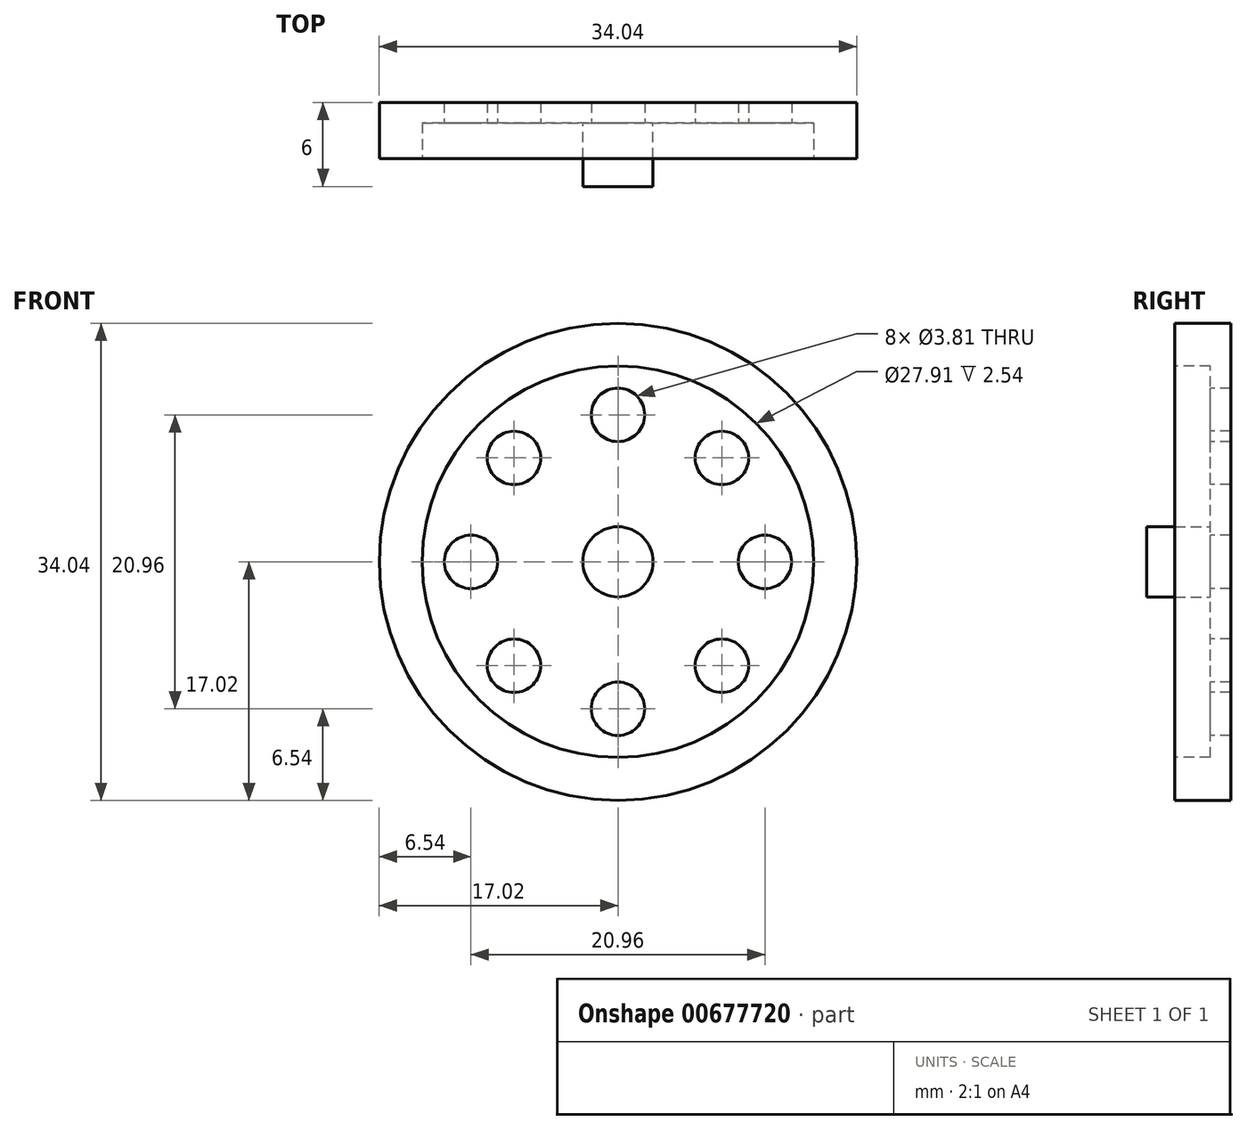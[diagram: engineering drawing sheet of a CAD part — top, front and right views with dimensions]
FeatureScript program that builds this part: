
annotation { "Feature Type Name" : "Feature", "Feature Type Description" : "" }
export const myFeature = defineFeature(function(context is Context, id is Id, definition is map)
    precondition{}
    {
        {
            var Q0;
            Q0=qCreatedBy(makeId("Front.planeOp"),FACE);
            var sketch = newSketch(context, id + "F0", { "sketchPlane" : qUnion([Q0])});
            skCircle(sketch, "E0", {"center": v(0, 0) * mm, "radius": 17.02 * mm});
            skSolve(sketch);
        }
        {
            var Q0;
            Q0 = qSketchRegion(id + "F0", true);
            extrude(context, id + "F1", {"entities" : qUnion([Q0]), "oppositeDirection" : true, "depth" : 4 * mm, "offsetDistance" : 25 * mm});
        }
        {
            var Q0;
            Q0=makeQuery(id+"F1.opExtrude","CAP_FACE",FACE,{"disambiguationData":[OSD([sQuery(id+"F0.wireOp",EDGE,"E0")])],"isStart":true});
            var sketch = newSketch(context, id + "F2", { "sketchPlane" : qUnion([Q0])});
            skCircle(sketch, "E1", {"center": v(0, 0) * mm, "radius": 6 * mm});
            skSolve(sketch);
        }
        {
            var Q0;
            Q0=sQuery(id+"F2.wireOp",EDGE,"E1");
            extrude(context, id + "F3", {"bodyType" : ToolBodyType.SURFACE, "surfaceEntities" : qUnion([Q0]), "oppositeDirection" : true, "depth" : 4 * mm, "offsetDistance" : 25 * mm});
        }
        {
            var Q0;
            Q0=qCreatedBy(makeId("Front.planeOp"),FACE);
            var sketch = newSketch(context, id + "F4", { "sketchPlane" : qUnion([Q0])});
            skCircle(sketch, "E2", {"center": v(0, 0) * mm, "radius": 2.5 * mm});
            skSolve(sketch);
        }
        {
            var Q0;
            Q0 = qSketchRegion(id + "F4", true);
            extrude(context, id + "F5", {"entities" : qUnion([Q0]), "operationType" : NewBodyOperationType.ADD, "depth" : 2 * mm, "offsetDistance" : 25 * mm});
        }
        {
            var Q0;
            Q0=makeQuery(id+"F1.opExtrude","CAP_FACE",FACE,{"disambiguationData":[OSD([sQuery(id+"F0.wireOp",EDGE,"E0")])],"isStart":false});
            var sketch = newSketch(context, id + "F6", { "sketchPlane" : qUnion([Q0])});
            skSolve(sketch);
        }
        {
            var Q0;
            Q0=makeQuery(id+"F1.opExtrude","CAP_FACE",FACE,{"disambiguationData":[OSD([sQuery(id+"F0.wireOp",EDGE,"E0")])],"isStart":true});
            var sketch = newSketch(context, id + "F7", { "sketchPlane" : qUnion([Q0])});
            skCircle(sketch, "E3", {"center": v(0, 10.48) * mm, "radius": 1.9 * mm});
            skCircle(sketch, "E4.1.0", {"center": v(-7.41, 7.41) * mm, "radius": 1.9 * mm});
            skCircle(sketch, "E4.2.0", {"center": v(-10.48, 0) * mm, "radius": 1.9 * mm});
            skCircle(sketch, "E4.3.0", {"center": v(-7.41, -7.41) * mm, "radius": 1.9 * mm});
            skCircle(sketch, "E4.4.0", {"center": v(0, -10.48) * mm, "radius": 1.9 * mm});
            skCircle(sketch, "E4.5.0", {"center": v(7.41, -7.41) * mm, "radius": 1.9 * mm});
            skCircle(sketch, "E4.6.0", {"center": v(10.48, 0) * mm, "radius": 1.9 * mm});
            skCircle(sketch, "E4.7.0", {"center": v(7.41, 7.41) * mm, "radius": 1.9 * mm});
            skPoint(sketch, "E4.center", {"position": v(0, 0) * mm});
            skSolve(sketch);
        }
        {
            var Q0;
            Q0=makeQuery(id+"F7.imprint","IMPRINT",FACE,{"disambiguationData":[TD([[makeQuery(id+"F7.imprint","IMPRINT",EDGE,{"derivedFrom":sQuery(id+"F7.wireOp",EDGE,"E4.1.0")}),1.0]])]});
            var Q1;
            Q1=makeQuery(id+"F7.imprint","IMPRINT",FACE,{"disambiguationData":[TD([[makeQuery(id+"F7.imprint","IMPRINT",EDGE,{"derivedFrom":sQuery(id+"F7.wireOp",EDGE,"E3")}),1.0]])]});
            var Q2;
            Q2=makeQuery(id+"F7.imprint","IMPRINT",FACE,{"disambiguationData":[TD([[makeQuery(id+"F7.imprint","IMPRINT",EDGE,{"derivedFrom":sQuery(id+"F7.wireOp",EDGE,"E4.7.0")}),1.0]])]});
            var Q3;
            Q3=makeQuery(id+"F7.imprint","IMPRINT",FACE,{"disambiguationData":[TD([[makeQuery(id+"F7.imprint","IMPRINT",EDGE,{"derivedFrom":sQuery(id+"F7.wireOp",EDGE,"E4.6.0")}),1.0]])]});
            var Q4;
            Q4=makeQuery(id+"F7.imprint","IMPRINT",FACE,{"disambiguationData":[TD([[makeQuery(id+"F7.imprint","IMPRINT",EDGE,{"derivedFrom":sQuery(id+"F7.wireOp",EDGE,"E4.5.0")}),1.0]])]});
            var Q5;
            Q5=makeQuery(id+"F7.imprint","IMPRINT",FACE,{"disambiguationData":[TD([[makeQuery(id+"F7.imprint","IMPRINT",EDGE,{"derivedFrom":sQuery(id+"F7.wireOp",EDGE,"E4.4.0")}),1.0]])]});
            var Q6;
            Q6=makeQuery(id+"F7.imprint","IMPRINT",FACE,{"disambiguationData":[TD([[makeQuery(id+"F7.imprint","IMPRINT",EDGE,{"derivedFrom":sQuery(id+"F7.wireOp",EDGE,"E4.3.0")}),1.0]])]});
            var Q7;
            Q7=makeQuery(id+"F7.imprint","IMPRINT",FACE,{"disambiguationData":[TD([[makeQuery(id+"F7.imprint","IMPRINT",EDGE,{"derivedFrom":sQuery(id+"F7.wireOp",EDGE,"E4.2.0")}),1.0]])]});
            extrude(context, id + "F8", {"entities" : qUnion([Q0, Q1, Q2, Q3, Q4, Q5, Q6, Q7]), "operationType" : NewBodyOperationType.REMOVE, "oppositeDirection" : true, "depth" : 25.4 * mm, "offsetDistance" : 25.4 * mm});
        }
        {
            var Q0;
            Q0=makeQuery(id+"F1.opExtrude","CAP_FACE",FACE,{"disambiguationData":[OSD([sQuery(id+"F0.wireOp",EDGE,"E0")])],"isStart":true});
            var sketch = newSketch(context, id + "F9", { "sketchPlane" : qUnion([Q0])});
            skCircle(sketch, "E5", {"center": v(0, 0) * mm, "radius": 13.96 * mm});
            skSolve(sketch);
        }
        {
            var Q0;
            Q0=makeQuery(id+"F9.imprint","IMPRINT",FACE,{"disambiguationData":[TD([[makeQuery(id+"F9.imprint","IMPRINT",EDGE,{"derivedFrom":sQuery(id+"F9.wireOp",EDGE,"E5")}),1.0]])]});
            extrude(context, id + "F10", {"entities" : qUnion([Q0]), "operationType" : NewBodyOperationType.REMOVE, "oppositeDirection" : true, "depth" : 2.54 * mm, "offsetDistance" : 25.4 * mm});
        }
        {
            var Q0;
            Q0=makeQuery(id+"F6.imprint","IMPRINT",FACE,{"disambiguationData":[TD([[makeQuery(id+"F6.imprint","IMPRINT",EDGE,{"derivedFrom":makeQuery(id+"F1.opExtrude","CAP_EDGE",EDGE,{"disambiguationData":[OSD([sQuery(id+"F0.wireOp",EDGE,"E0")])],"isStart":false})}),-1.0]])]});
            var sketch = newSketch(context, id + "F11", { "sketchPlane" : qUnion([Q0])});
            skCircle(sketch, "E6", {"center": v(0, 0) * mm, "radius": 3.46 * mm});
            skSolve(sketch);
        }
        {
            var Q0;
            Q0=sQuery(id+"F11.wireOp",EDGE,"E6");
            extrude(context, id + "F12", {"bodyType" : ToolBodyType.SURFACE, "surfaceEntities" : qUnion([Q0]), "depth" : 12.7 * mm, "offsetDistance" : 25.4 * mm});
        }
    });
